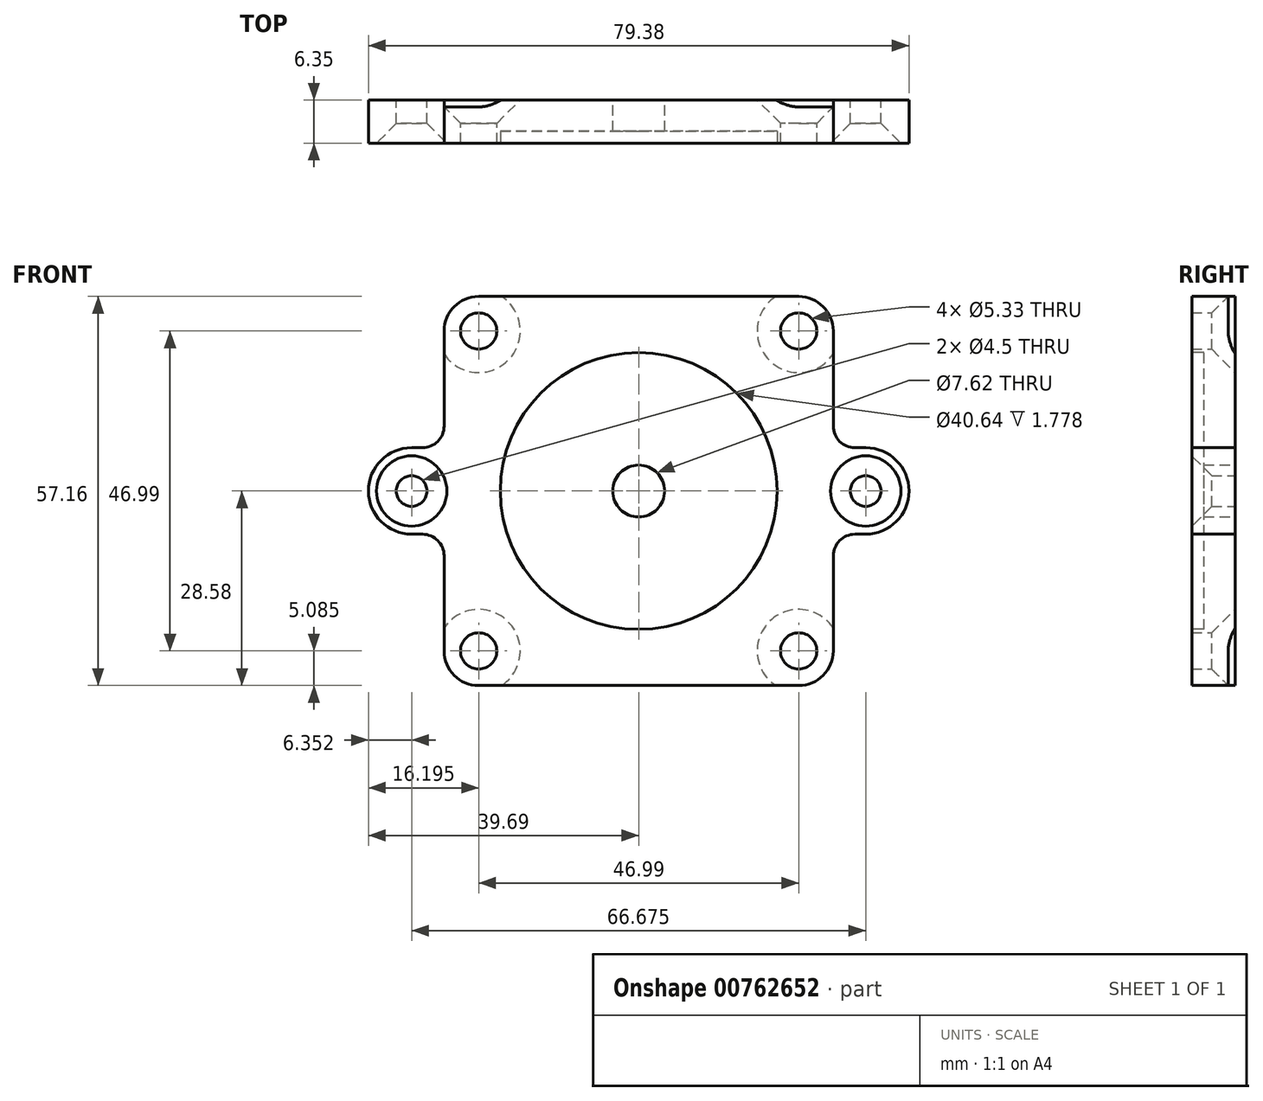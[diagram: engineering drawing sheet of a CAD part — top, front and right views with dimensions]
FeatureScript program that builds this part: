
annotation { "Feature Type Name" : "Feature", "Feature Type Description" : "" }
export const myFeature = defineFeature(function(context is Context, id is Id, definition is map)
    precondition{}
    {
        {
            var Q0;
            Q0=qCreatedBy(makeId("Front.planeOp"),FACE);
            var sketch = newSketch(context, id + "F0", { "sketchPlane" : qUnion([Q0])});
            skLineSegment(sketch, "E0.bottom", {"start": v(23.5, -28.58) * mm, "end": v(-23.5, -28.58) * mm});
            skLineSegment(sketch, "E0.top", {"start": v(23.5, 28.58) * mm, "end": v(-23.5, 28.57) * mm});
            skLineSegment(sketch, "E0.left", {"start": v(28.58, -23.5) * mm, "end": v(28.58, -9.53) * mm});
            skLineSegment(sketch, "E0.right", {"start": v(-28.58, -23.5) * mm, "end": v(-28.58, -9.53) * mm});
            skPoint(sketch, "E0.middle", {"position": v(0, 0) * mm});
            skArc(sketch, "E1", {"start": v(33.34, -6.35) * mm, "mid": v(39.69, 0) * mm, "end": v(33.34, 6.35) * mm});
            skPoint(sketch, "E1.centerSnap0", {"position": v(28.58, 0) * mm});
            skCircle(sketch, "E2", {"center": v(33.34, 0) * mm, "radius": 2.25 * mm});
            skArc(sketch, "E3", {"start": v(-33.34, 6.35) * mm, "mid": v(-39.69, 0) * mm, "end": v(-33.34, -6.35) * mm});
            skCircle(sketch, "E4", {"center": v(-33.34, 0) * mm, "radius": 2.25 * mm});
            skLineSegment(sketch, "E5", {"start": v(-33.34, -6.35) * mm, "end": v(-31.75, -6.35) * mm});
            skLineSegment(sketch, "E6", {"start": v(-33.34, 6.35) * mm, "end": v(-31.75, 6.35) * mm});
            skLineSegment(sketch, "E7.trimOffspring", {"start": v(-28.58, 9.53) * mm, "end": v(-28.57, 23.5) * mm});
            skLineSegment(sketch, "E8", {"start": v(33.34, -6.35) * mm, "end": v(31.75, -6.35) * mm});
            skLineSegment(sketch, "E9", {"start": v(33.34, 6.35) * mm, "end": v(31.75, 6.35) * mm});
            skLineSegment(sketch, "E10.trimOffspring", {"start": v(28.58, 9.53) * mm, "end": v(28.58, 23.5) * mm});
            skPoint(sketch, "E11.visualSharp", {"position": v(-28.58, 28.57) * mm});
            skArc(sketch, "E11.filletArc", {"start": v(-23.5, 28.57) * mm, "mid": v(-27.09, 27.09) * mm, "end": v(-28.58, 23.5) * mm});
            skPoint(sketch, "E12.visualSharp", {"position": v(28.58, 28.58) * mm});
            skArc(sketch, "E12.filletArc", {"start": v(28.58, 23.5) * mm, "mid": v(27.09, 27.09) * mm, "end": v(23.5, 28.58) * mm});
            skPoint(sketch, "E13.visualSharp", {"position": v(-28.58, -28.58) * mm});
            skArc(sketch, "E13.filletArc", {"start": v(-28.58, -23.5) * mm, "mid": v(-27.09, -27.09) * mm, "end": v(-23.5, -28.58) * mm});
            skPoint(sketch, "E14.visualSharp", {"position": v(28.58, -28.58) * mm});
            skArc(sketch, "E14.filletArc", {"start": v(23.5, -28.58) * mm, "mid": v(27.09, -27.09) * mm, "end": v(28.58, -23.5) * mm});
            skPoint(sketch, "E15.visualSharp", {"position": v(-28.58, -6.35) * mm});
            skArc(sketch, "E15.filletArc", {"start": v(-28.57, -9.53) * mm, "mid": v(-29.5, -7.28) * mm, "end": v(-31.75, -6.35) * mm});
            skPoint(sketch, "E16.visualSharp", {"position": v(-28.58, 6.35) * mm});
            skArc(sketch, "E16.filletArc", {"start": v(-31.75, 6.35) * mm, "mid": v(-29.5, 7.28) * mm, "end": v(-28.58, 9.53) * mm});
            skPoint(sketch, "E17.visualSharp", {"position": v(28.58, -6.35) * mm});
            skArc(sketch, "E17.filletArc", {"start": v(31.75, -6.35) * mm, "mid": v(29.5, -7.28) * mm, "end": v(28.57, -9.53) * mm});
            skPoint(sketch, "E18.visualSharp", {"position": v(28.58, 6.35) * mm});
            skArc(sketch, "E18.filletArc", {"start": v(28.57, 9.53) * mm, "mid": v(29.5, 7.28) * mm, "end": v(31.75, 6.35) * mm});
            skCircle(sketch, "E19", {"center": v(0, 0) * mm, "radius": 3.81 * mm});
            skCircle(sketch, "E20", {"center": v(23.5, 23.5) * mm, "radius": 2.67 * mm});
            skCircle(sketch, "E21", {"center": v(-23.5, 23.5) * mm, "radius": 2.67 * mm});
            skCircle(sketch, "E22", {"center": v(-23.5, -23.5) * mm, "radius": 2.67 * mm});
            skCircle(sketch, "E23", {"center": v(23.5, -23.5) * mm, "radius": 2.67 * mm});
            skSolve(sketch);
        }
        {
            var Q0;
            Q0 = qSketchRegion(id + "F0", true);
            var Q1;
            Q1=makeQuery(id+"F0.imprint","IMPRINT",FACE,{"disambiguationData":[TD([[makeQuery(id+"F0.imprint","IMPRINT",EDGE,{"derivedFrom":sQuery(id+"F0.wireOp",EDGE,"E0.bottom")}),-1.0]])]});
            extrude(context, id + "F1", {"entities" : qUnion([Q0, Q1]), "depth" : 6.35 * mm, "offsetDistance" : 25.4 * mm});
        }
        {
            var Q0;
            Q0=makeQuery(id+"F1.opExtrude","CAP_FACE",FACE,{"disambiguationData":[OSD([sQuery(id+"F0.wireOp",EDGE,"E0.bottom"),sQuery(id+"F0.wireOp",EDGE,"E0.top"),sQuery(id+"F0.wireOp",EDGE,"E0.left"),sQuery(id+"F0.wireOp",EDGE,"E0.right"),sQuery(id+"F0.wireOp",EDGE,"E1"),sQuery(id+"F0.wireOp",EDGE,"E2"),sQuery(id+"F0.wireOp",EDGE,"E3"),sQuery(id+"F0.wireOp",EDGE,"E4"),sQuery(id+"F0.wireOp",EDGE,"E5"),sQuery(id+"F0.wireOp",EDGE,"E6"),sQuery(id+"F0.wireOp",EDGE,"E7.trimOffspring"),sQuery(id+"F0.wireOp",EDGE,"E8"),sQuery(id+"F0.wireOp",EDGE,"E9"),sQuery(id+"F0.wireOp",EDGE,"E10.trimOffspring"),sQuery(id+"F0.wireOp",EDGE,"E11.filletArc"),sQuery(id+"F0.wireOp",EDGE,"E12.filletArc"),sQuery(id+"F0.wireOp",EDGE,"E13.filletArc"),sQuery(id+"F0.wireOp",EDGE,"E14.filletArc"),sQuery(id+"F0.wireOp",EDGE,"E15.filletArc"),sQuery(id+"F0.wireOp",EDGE,"E16.filletArc"),sQuery(id+"F0.wireOp",EDGE,"E17.filletArc"),sQuery(id+"F0.wireOp",EDGE,"E18.filletArc"),sQuery(id+"F0.wireOp",EDGE,"E19"),sQuery(id+"F0.wireOp",EDGE,"E20"),sQuery(id+"F0.wireOp",EDGE,"E21"),sQuery(id+"F0.wireOp",EDGE,"E22"),sQuery(id+"F0.wireOp",EDGE,"E23")])],"isStart":false});
            var sketch = newSketch(context, id + "F2", { "sketchPlane" : qUnion([Q0])});
            skCircle(sketch, "E24", {"center": v(0, 0) * mm, "radius": 20.32 * mm});
            skSolve(sketch);
        }
        {
            var Q0;
            Q0 = qSketchRegion(id + "F2", true);
            var Q1;
            Q1=makeQuery(id+"F2.imprint","IMPRINT",FACE,{"disambiguationData":[TD([[makeQuery(id+"F2.imprint","IMPRINT",EDGE,{"derivedFrom":sQuery(id+"F2.wireOp",EDGE,"E24")}),1.0]])]});
            extrude(context, id + "F3", {"entities" : qUnion([Q0, Q1]), "operationType" : NewBodyOperationType.REMOVE, "oppositeDirection" : true, "depth" : 1.78 * mm, "offsetDistance" : 25.4 * mm});
        }
        {
            var Q0;
            Q0=makeQuery(id+"F1.opExtrude","CAP_EDGE",EDGE,{"disambiguationData":[OSD([sQuery(id+"F0.wireOp",EDGE,"E4")])],"isStart":false});
            var Q1;
            Q1=makeQuery(id+"F1.opExtrude","CAP_EDGE",EDGE,{"disambiguationData":[OSD([sQuery(id+"F0.wireOp",EDGE,"E2")])],"isStart":false});
            chamfer(context, id + "F4", {"entities" : qUnion([Q0, Q1]), "width" : 2.92 * mm, "tangentPropagation" : true});
        }
        {
            var Q0;
            Q0=makeQuery(id+"F1.opExtrude","CAP_EDGE",EDGE,{"disambiguationData":[OSD([sQuery(id+"F0.wireOp",EDGE,"E20")])],"isStart":true});
            var Q1;
            Q1=makeQuery(id+"F1.opExtrude","CAP_EDGE",EDGE,{"disambiguationData":[OSD([sQuery(id+"F0.wireOp",EDGE,"E21")])],"isStart":true});
            var Q2;
            Q2=makeQuery(id+"F1.opExtrude","CAP_EDGE",EDGE,{"disambiguationData":[OSD([sQuery(id+"F0.wireOp",EDGE,"E23")])],"isStart":true});
            var Q3;
            Q3=makeQuery(id+"F1.opExtrude","CAP_EDGE",EDGE,{"disambiguationData":[OSD([sQuery(id+"F0.wireOp",EDGE,"E22")])],"isStart":true});
            chamfer(context, id + "F5", {"entities" : qUnion([Q0, Q1, Q2, Q3]), "width" : 3.43 * mm, "tangentPropagation" : true});
        }
    });
